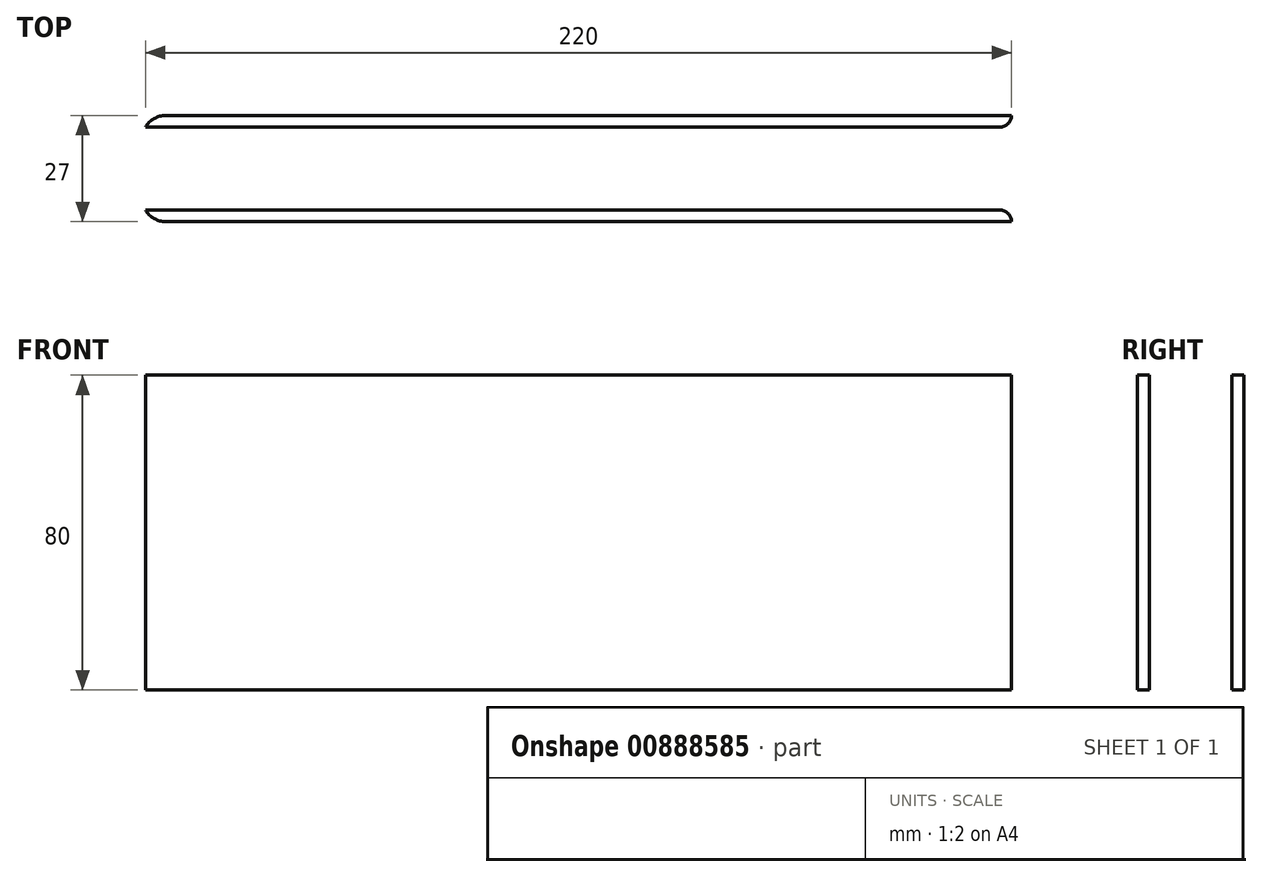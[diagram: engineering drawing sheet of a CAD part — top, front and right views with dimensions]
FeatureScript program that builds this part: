
annotation { "Feature Type Name" : "Feature", "Feature Type Description" : "" }
export const myFeature = defineFeature(function(context is Context, id is Id, definition is map)
    precondition{}
    {
        {
            var Q0;
            Q0=qCreatedBy(makeId("Top.planeOp"),FACE);
            var sketch = newSketch(context, id + "F0", { "sketchPlane" : qUnion([Q0])});
            skLineSegment(sketch, "E0.bottom", {"start": v(-110, -1.5) * mm, "end": v(110, -1.5) * mm});
            skLineSegment(sketch, "E0.top", {"start": v(-110, 1.5) * mm, "end": v(110, 1.5) * mm});
            skLineSegment(sketch, "E0.left", {"start": v(-110, -1.5) * mm, "end": v(-110, 1.5) * mm});
            skLineSegment(sketch, "E0.right", {"start": v(110, -1.5) * mm, "end": v(110, 1.5) * mm});
            skPoint(sketch, "E0.middle", {"position": v(0, 0) * mm});
            skLineSegment(sketch, "E1.bottom", {"start": v(-110, -1.5) * mm, "end": v(-107, -1.5) * mm});
            skLineSegment(sketch, "E1.top", {"start": v(-110, -22.5) * mm, "end": v(-107, -22.5) * mm});
            skLineSegment(sketch, "E1.left", {"start": v(-110, -1.5) * mm, "end": v(-110, -22.5) * mm});
            skLineSegment(sketch, "E1.right", {"start": v(-107, -1.5) * mm, "end": v(-107, -22.5) * mm});
            skLineSegment(sketch, "E2.bottom", {"start": v(-110, -22.5) * mm, "end": v(110, -22.5) * mm});
            skLineSegment(sketch, "E2.top", {"start": v(-110, -25.5) * mm, "end": v(110, -25.5) * mm});
            skLineSegment(sketch, "E2.left", {"start": v(-110, -22.5) * mm, "end": v(-110, -25.5) * mm});
            skLineSegment(sketch, "E2.right", {"start": v(110, -22.5) * mm, "end": v(110, -25.5) * mm});
            skSolve(sketch);
        }
        {
            var Q0;
            Q0=makeQuery(id+"F0.imprint","IMPRINT",FACE,{"disambiguationData":[TD([[makeQuery(id+"F0.imprint","IMPRINT",EDGE,{"derivedFrom":sQuery(id+"F0.wireOp",EDGE,"E0.bottom")}),1.0]])]});
            var Q1;
            Q1=makeQuery(id+"F0.imprint","IMPRINT",FACE,{"disambiguationData":[TD([[makeQuery(id+"F0.imprint","IMPRINT",EDGE,{"derivedFrom":sQuery(id+"F0.wireOp",EDGE,"E1.bottom")}),-1.0]])]});
            var Q2;
            Q2=makeQuery(id+"F0.imprint","IMPRINT",FACE,{"disambiguationData":[TD([[makeQuery(id+"F0.imprint","IMPRINT",EDGE,{"derivedFrom":sQuery(id+"F0.wireOp",EDGE,"E2.top")}),1.0]])]});
            extrude(context, id + "F1", {"entities" : qUnion([Q0, Q1, Q2]), "depth" : 80 * mm, "offsetDistance" : 25.4 * mm});
        }
        {
            var Q0;
            Q0=makeQuery(id+"F1.opExtrude","SWEPT_EDGE",EDGE,{"disambiguationData":[OSD([sQuery(id+"F0.wireOp",EDGE,"E0.bottom"),sQuery(id+"F0.wireOp",EDGE,"E1.bottom"),sQuery(id+"F0.wireOp",EDGE,"E1.right")])]});
            var Q1;
            Q1=makeQuery(id+"F1.opExtrude","SWEPT_EDGE",EDGE,{"disambiguationData":[OSD([sQuery(id+"F0.wireOp",EDGE,"E1.right"),sQuery(id+"F0.wireOp",EDGE,"E2.bottom")])]});
            fillet(context, id + "F2", {"entities" : qUnion([Q0, Q1]), "radius" : 3 * mm, "tangentPropagation" : true, "allowEdgeOverflow" : false});
        }
        {
            var Q0;
            Q0=makeQuery(id+"F1.opExtrude","SWEPT_EDGE",EDGE,{"disambiguationData":[OSD([sQuery(id+"F0.wireOp",EDGE,"E2.top"),sQuery(id+"F0.wireOp",EDGE,"E2.left")])]});
            var Q1;
            Q1=makeQuery(id+"F1.opExtrude","SWEPT_EDGE",EDGE,{"disambiguationData":[OSD([sQuery(id+"F0.wireOp",EDGE,"E0.top"),sQuery(id+"F0.wireOp",EDGE,"E0.left")])]});
            fillet(context, id + "F3", {"entities" : qUnion([Q0, Q1]), "radius" : 6 * mm, "tangentPropagation" : true, "allowEdgeOverflow" : false});
        }
    });
